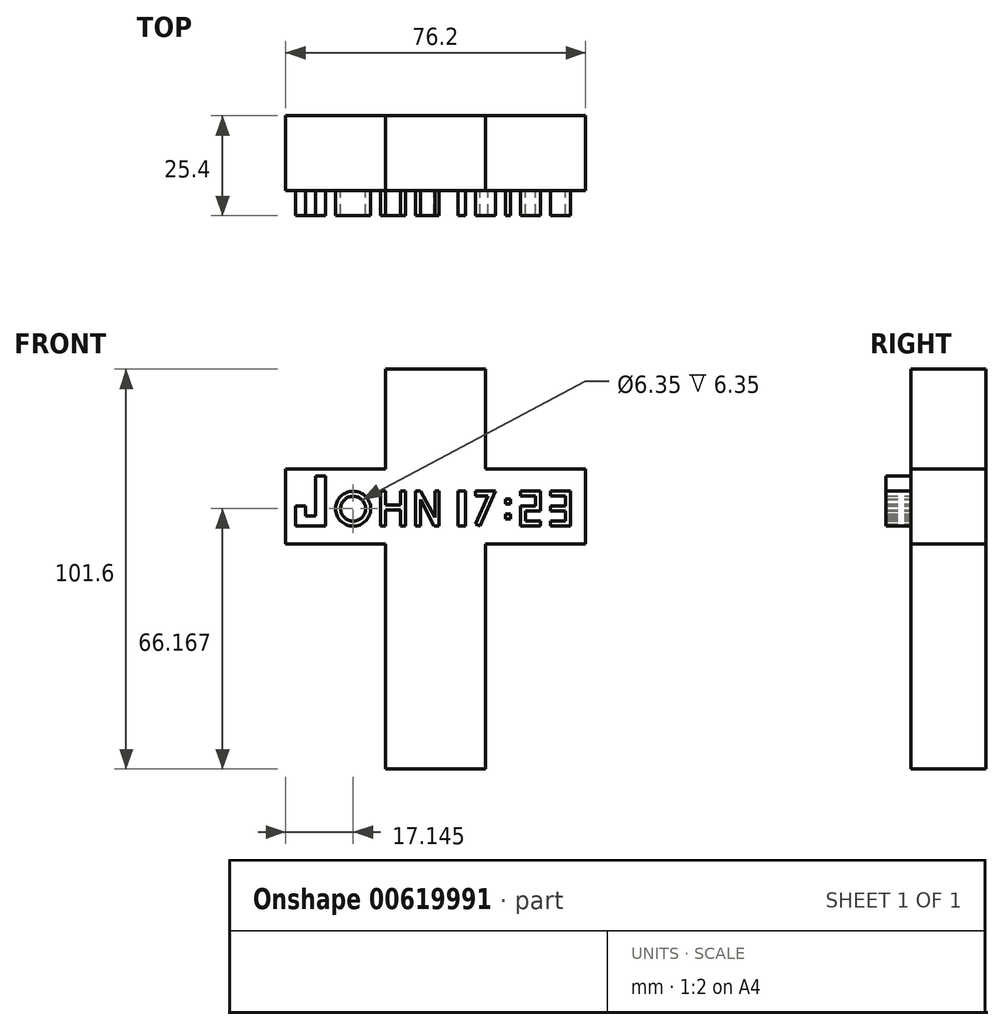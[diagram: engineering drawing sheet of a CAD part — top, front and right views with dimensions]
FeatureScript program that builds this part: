
annotation { "Feature Type Name" : "Feature", "Feature Type Description" : "" }
export const myFeature = defineFeature(function(context is Context, id is Id, definition is map)
    precondition{}
    {
        {
            var Q0;
            Q0=qCreatedBy(makeId("Front.planeOp"),FACE);
            var sketch = newSketch(context, id + "F0", { "sketchPlane" : qUnion([Q0])});
            skLineSegment(sketch, "E0", {"start": v(0, 0) * mm, "end": v(-25.4, 0) * mm});
            skLineSegment(sketch, "E1", {"start": v(-25.4, 0) * mm, "end": v(-25.4, 101.6) * mm});
            skLineSegment(sketch, "E2", {"start": v(-25.4, 101.6) * mm, "end": v(0, 101.6) * mm});
            skLineSegment(sketch, "E3", {"start": v(0, 101.6) * mm, "end": v(0, 0) * mm});
            skLineSegment(sketch, "E4", {"start": v(-25.4, 76.2) * mm, "end": v(-50.8, 76.2) * mm});
            skLineSegment(sketch, "E5", {"start": v(-50.8, 76.2) * mm, "end": v(-50.8, 57.15) * mm});
            skLineSegment(sketch, "E6", {"start": v(-50.8, 57.15) * mm, "end": v(-25.4, 57.15) * mm});
            skLineSegment(sketch, "E7", {"start": v(0, 76.2) * mm, "end": v(25.4, 76.2) * mm});
            skLineSegment(sketch, "E8", {"start": v(25.4, 76.2) * mm, "end": v(25.4, 57.15) * mm});
            skLineSegment(sketch, "E9", {"start": v(25.4, 57.15) * mm, "end": v(0, 57.15) * mm});
            skSolve(sketch);
        }
        {
            var Q0;
            Q0 = qSketchRegion(id + "F0", true);
            extrude(context, id + "F1", {"entities" : qUnion([Q0]), "depth" : 19.05 * mm, "offsetDistance" : 25.4 * mm});
        }
        {
            var Q0;
            Q0=qCreatedBy(makeId("Front.planeOp"),FACE);
            cPlane(context, id + "F2", {"entities" : qUnion([Q0]), "cplaneType" : CPlaneType.OFFSET, "offset" : 19.05 * mm, "width" : 152.4 * mm, "height" : 152.4 * mm});
        }
        {
            var Q0;
            Q0=qCreatedBy(id+"F2.planeOp",FACE);
            var sketch = newSketch(context, id + "F3", { "sketchPlane" : qUnion([Q0])});
            skLineSegment(sketch, "E10", {"start": v(-48.26, 66.8) * mm, "end": v(-45.72, 66.8) * mm});
            skLineSegment(sketch, "E11", {"start": v(-43.18, 74.42) * mm, "end": v(-40.64, 74.42) * mm});
            skLineSegment(sketch, "E12", {"start": v(-43.18, 74.42) * mm, "end": v(-43.18, 64.26) * mm});
            skLineSegment(sketch, "E13", {"start": v(-45.72, 66.8) * mm, "end": v(-45.72, 64.26) * mm});
            skLineSegment(sketch, "E14", {"start": v(-45.72, 64.26) * mm, "end": v(-43.18, 64.26) * mm});
            skLineSegment(sketch, "E15", {"start": v(-48.26, 66.8) * mm, "end": v(-48.26, 61.72) * mm});
            skLineSegment(sketch, "E16", {"start": v(-48.26, 61.72) * mm, "end": v(-40.64, 61.72) * mm});
            skLineSegment(sketch, "E17", {"start": v(-40.64, 74.42) * mm, "end": v(-40.64, 61.72) * mm});
            skSolve(sketch);
        }
        {
            var Q0;
            Q0=makeQuery(id+"F3.imprint","IMPRINT",FACE,{"disambiguationData":[TD([[makeQuery(id+"F3.imprint","IMPRINT",EDGE,{"derivedFrom":sQuery(id+"F3.wireOp",EDGE,"E10")}),-1.0]])]});
            extrude(context, id + "F4", {"entities" : qUnion([Q0]), "operationType" : NewBodyOperationType.ADD, "depth" : 6.35 * mm, "offsetDistance" : 25.4 * mm});
        }
        {
            var Q0;
            Q0=qCreatedBy(id+"F2.planeOp",FACE);
            var sketch = newSketch(context, id + "F5", { "sketchPlane" : qUnion([Q0])});
            skCircle(sketch, "E18", {"center": v(-33.66, 66.17) * mm, "radius": 4.45 * mm});
            skCircle(sketch, "E19", {"center": v(-33.66, 66.17) * mm, "radius": 3.17 * mm});
            skSolve(sketch);
        }
        {
            var Q0;
            Q0=makeQuery(id+"F5.imprint","IMPRINT",FACE,{"disambiguationData":[TD([[makeQuery(id+"F5.imprint","IMPRINT",EDGE,{"derivedFrom":sQuery(id+"F5.wireOp",EDGE,"E18")}),1.0]])]});
            extrude(context, id + "F6", {"entities" : qUnion([Q0]), "operationType" : NewBodyOperationType.ADD, "depth" : 6.35 * mm, "offsetDistance" : 25.4 * mm});
        }
        {
            var Q0;
            Q0=qCreatedBy(id+"F2.planeOp",FACE);
            var sketch = newSketch(context, id + "F7", { "sketchPlane" : qUnion([Q0])});
            skLineSegment(sketch, "E20", {"start": v(-26.67, 70.61) * mm, "end": v(-25.4, 70.61) * mm});
            skLineSegment(sketch, "E21", {"start": v(-25.4, 70.61) * mm, "end": v(-25.4, 61.72) * mm});
            skLineSegment(sketch, "E22", {"start": v(-25.4, 61.72) * mm, "end": v(-26.67, 61.72) * mm});
            skLineSegment(sketch, "E23", {"start": v(-26.67, 61.72) * mm, "end": v(-26.67, 70.61) * mm});
            skLineSegment(sketch, "E24", {"start": v(-25.4, 67.06) * mm, "end": v(-21.6, 67.06) * mm});
            skLineSegment(sketch, "E25", {"start": v(-21.6, 67.06) * mm, "end": v(-21.6, 65.79) * mm});
            skLineSegment(sketch, "E26", {"start": v(-21.6, 65.79) * mm, "end": v(-25.4, 65.79) * mm});
            skLineSegment(sketch, "E27", {"start": v(-21.6, 67.06) * mm, "end": v(-21.6, 70.61) * mm});
            skLineSegment(sketch, "E28", {"start": v(-21.6, 70.61) * mm, "end": v(-20.32, 70.61) * mm});
            skLineSegment(sketch, "E29", {"start": v(-20.32, 70.61) * mm, "end": v(-20.32, 61.72) * mm});
            skLineSegment(sketch, "E30", {"start": v(-20.32, 61.72) * mm, "end": v(-21.6, 61.72) * mm});
            skLineSegment(sketch, "E31", {"start": v(-21.6, 61.72) * mm, "end": v(-21.6, 65.79) * mm});
            skSolve(sketch);
        }
        {
            var Q0;
            Q0 = qSketchRegion(id + "F7", true);
            extrude(context, id + "F8", {"entities" : qUnion([Q0]), "operationType" : NewBodyOperationType.ADD, "depth" : 6.35 * mm, "offsetDistance" : 25.4 * mm});
        }
        {
            var Q0;
            Q0=qCreatedBy(id+"F2.planeOp",FACE);
            var sketch = newSketch(context, id + "F9", { "sketchPlane" : qUnion([Q0])});
            skLineSegment(sketch, "E32", {"start": v(-17.78, 61.72) * mm, "end": v(-17.78, 70.61) * mm});
            skLineSegment(sketch, "E33", {"start": v(-17.78, 70.61) * mm, "end": v(-16.51, 70.61) * mm});
            skLineSegment(sketch, "E34", {"start": v(-16.51, 70.61) * mm, "end": v(-16.51, 61.72) * mm});
            skLineSegment(sketch, "E35", {"start": v(-16.51, 61.72) * mm, "end": v(-17.78, 61.72) * mm});
            skLineSegment(sketch, "E36", {"start": v(-11.78, 61.72) * mm, "end": v(-13.05, 61.72) * mm});
            skLineSegment(sketch, "E37", {"start": v(-13.05, 61.72) * mm, "end": v(-16.51, 68.51) * mm});
            skLineSegment(sketch, "E38", {"start": v(-11.78, 61.72) * mm, "end": v(-11.78, 70.61) * mm});
            skLineSegment(sketch, "E39", {"start": v(-11.78, 70.61) * mm, "end": v(-12.92, 70.61) * mm});
            skLineSegment(sketch, "E40", {"start": v(-12.92, 70.61) * mm, "end": v(-12.92, 61.72) * mm});
            skLineSegment(sketch, "E41", {"start": v(-16.51, 70.61) * mm, "end": v(-12.92, 63.9) * mm});
            skSolve(sketch);
        }
        {
            var Q0;
            Q0 = qSketchRegion(id + "F9", true);
            extrude(context, id + "F10", {"entities" : qUnion([Q0]), "operationType" : NewBodyOperationType.ADD, "depth" : 6.35 * mm, "offsetDistance" : 25.4 * mm});
        }
        {
            var Q0;
            Q0=qCreatedBy(id+"F2.planeOp",FACE);
            var sketch = newSketch(context, id + "F11", { "sketchPlane" : qUnion([Q0])});
            skLineSegment(sketch, "E42", {"start": v(-6.97, 70.61) * mm, "end": v(-5.06, 70.61) * mm});
            skLineSegment(sketch, "E43", {"start": v(-5.06, 70.61) * mm, "end": v(-5.06, 61.72) * mm});
            skLineSegment(sketch, "E44", {"start": v(-5.06, 61.72) * mm, "end": v(-6.97, 61.72) * mm});
            skLineSegment(sketch, "E45", {"start": v(-6.97, 61.72) * mm, "end": v(-6.97, 70.61) * mm});
            skSolve(sketch);
        }
        {
            var Q0;
            Q0 = qSketchRegion(id + "F11", true);
            extrude(context, id + "F12", {"entities" : qUnion([Q0]), "operationType" : NewBodyOperationType.ADD, "depth" : 6.35 * mm, "offsetDistance" : 25.4 * mm});
        }
        {
            var Q0;
            Q0=qCreatedBy(id+"F2.planeOp",FACE);
            var sketch = newSketch(context, id + "F13", { "sketchPlane" : qUnion([Q0])});
            skLineSegment(sketch, "E46", {"start": v(-2.52, 70.61) * mm, "end": v(2.56, 70.61) * mm});
            skLineSegment(sketch, "E47", {"start": v(2.56, 70.61) * mm, "end": v(-1.42, 61.72) * mm});
            skLineSegment(sketch, "E48", {"start": v(-2.52, 70.61) * mm, "end": v(-2.52, 69.34) * mm});
            skLineSegment(sketch, "E49", {"start": v(-2.52, 69.34) * mm, "end": v(0.65, 69.34) * mm});
            skLineSegment(sketch, "E50", {"start": v(0.65, 69.34) * mm, "end": v(-2.52, 62.34) * mm});
            skLineSegment(sketch, "E51", {"start": v(-2.52, 62.34) * mm, "end": v(-1.42, 61.72) * mm});
            skSolve(sketch);
        }
        {
            var Q0;
            Q0 = qSketchRegion(id + "F13", true);
            extrude(context, id + "F14", {"entities" : qUnion([Q0]), "operationType" : NewBodyOperationType.ADD, "depth" : 6.35 * mm, "offsetDistance" : 25.4 * mm});
        }
        {
            var Q0;
            Q0=qCreatedBy(id+"F2.planeOp",FACE);
            var sketch = newSketch(context, id + "F15", { "sketchPlane" : qUnion([Q0])});
            skLineSegment(sketch, "E52.bottom", {"start": v(5.1, 68.58) * mm, "end": v(6.37, 68.58) * mm});
            skLineSegment(sketch, "E52.top", {"start": v(5.1, 67.31) * mm, "end": v(6.37, 67.31) * mm});
            skLineSegment(sketch, "E52.left", {"start": v(5.1, 68.58) * mm, "end": v(5.1, 67.31) * mm});
            skLineSegment(sketch, "E52.right", {"start": v(6.37, 68.58) * mm, "end": v(6.37, 67.31) * mm});
            skLineSegment(sketch, "E53.bottom", {"start": v(5.1, 64.77) * mm, "end": v(6.37, 64.77) * mm});
            skLineSegment(sketch, "E53.top", {"start": v(5.1, 63.5) * mm, "end": v(6.37, 63.5) * mm});
            skLineSegment(sketch, "E53.left", {"start": v(5.1, 64.77) * mm, "end": v(5.1, 63.5) * mm});
            skLineSegment(sketch, "E53.right", {"start": v(6.37, 64.77) * mm, "end": v(6.37, 63.5) * mm});
            skSolve(sketch);
        }
        {
            var Q0;
            Q0 = qSketchRegion(id + "F15", true);
            extrude(context, id + "F16", {"entities" : qUnion([Q0]), "operationType" : NewBodyOperationType.ADD, "depth" : 6.35 * mm, "offsetDistance" : 25.4 * mm});
        }
        {
            var Q0;
            Q0=qCreatedBy(id+"F2.planeOp",FACE);
            var sketch = newSketch(context, id + "F17", { "sketchPlane" : qUnion([Q0])});
            skLineSegment(sketch, "E54", {"start": v(8.9, 70.61) * mm, "end": v(13.99, 70.61) * mm});
            skLineSegment(sketch, "E55", {"start": v(13.99, 70.61) * mm, "end": v(13.99, 66.8) * mm});
            skLineSegment(sketch, "E56", {"start": v(13.99, 66.8) * mm, "end": v(8.9, 66.8) * mm});
            skLineSegment(sketch, "E57", {"start": v(8.9, 66.8) * mm, "end": v(8.9, 61.72) * mm});
            skLineSegment(sketch, "E58", {"start": v(8.9, 61.72) * mm, "end": v(13.99, 61.72) * mm});
            skLineSegment(sketch, "E59", {"start": v(13.99, 61.72) * mm, "end": v(13.99, 63) * mm});
            skLineSegment(sketch, "E60", {"start": v(13.99, 63) * mm, "end": v(10.18, 63) * mm});
            skLineSegment(sketch, "E61", {"start": v(10.18, 63) * mm, "end": v(10.18, 65.53) * mm});
            skLineSegment(sketch, "E62", {"start": v(10.18, 65.53) * mm, "end": v(13.99, 65.53) * mm});
            skLineSegment(sketch, "E63", {"start": v(13.99, 65.53) * mm, "end": v(13.99, 66.8) * mm});
            skLineSegment(sketch, "E64", {"start": v(8.9, 70.61) * mm, "end": v(8.9, 69.34) * mm});
            skLineSegment(sketch, "E65", {"start": v(8.9, 69.34) * mm, "end": v(12.72, 69.34) * mm});
            skLineSegment(sketch, "E66", {"start": v(12.72, 69.34) * mm, "end": v(12.72, 66.8) * mm});
            skSolve(sketch);
        }
        {
            var Q0;
            Q0 = qSketchRegion(id + "F17", true);
            extrude(context, id + "F18", {"entities" : qUnion([Q0]), "operationType" : NewBodyOperationType.ADD, "depth" : 6.35 * mm, "offsetDistance" : 25.4 * mm});
        }
        {
            var Q0;
            Q0=qCreatedBy(id+"F2.planeOp",FACE);
            var sketch = newSketch(context, id + "F19", { "sketchPlane" : qUnion([Q0])});
            skLineSegment(sketch, "E67", {"start": v(16.5, 69.34) * mm, "end": v(20.32, 69.34) * mm});
            skLineSegment(sketch, "E68", {"start": v(20.32, 65.53) * mm, "end": v(16.5, 65.53) * mm});
            skLineSegment(sketch, "E69", {"start": v(16.5, 65.53) * mm, "end": v(20.32, 65.53) * mm});
            skLineSegment(sketch, "E70", {"start": v(20.32, 61.72) * mm, "end": v(16.5, 61.72) * mm});
            skLineSegment(sketch, "E71", {"start": v(16.5, 61.72) * mm, "end": v(16.5, 63) * mm});
            skLineSegment(sketch, "E72", {"start": v(16.5, 63) * mm, "end": v(20.32, 63) * mm});
            skLineSegment(sketch, "E73", {"start": v(16.5, 65.53) * mm, "end": v(16.5, 66.8) * mm});
            skLineSegment(sketch, "E74", {"start": v(16.5, 66.8) * mm, "end": v(20.32, 66.8) * mm});
            skLineSegment(sketch, "E75", {"start": v(16.5, 69.34) * mm, "end": v(16.5, 70.61) * mm});
            skLineSegment(sketch, "E76", {"start": v(16.5, 70.61) * mm, "end": v(20.32, 70.61) * mm});
            skLineSegment(sketch, "E77", {"start": v(20.32, 70.61) * mm, "end": v(20.32, 69.34) * mm});
            skLineSegment(sketch, "E78", {"start": v(20.32, 70.61) * mm, "end": v(21.59, 70.61) * mm});
            skLineSegment(sketch, "E79", {"start": v(21.59, 70.61) * mm, "end": v(21.59, 61.72) * mm});
            skLineSegment(sketch, "E80", {"start": v(21.59, 61.72) * mm, "end": v(20.32, 61.72) * mm});
            skLineSegment(sketch, "E81", {"start": v(20.32, 61.72) * mm, "end": v(20.32, 63) * mm});
            skLineSegment(sketch, "E82", {"start": v(20.32, 65.53) * mm, "end": v(20.32, 63) * mm});
            skLineSegment(sketch, "E83", {"start": v(20.32, 65.53) * mm, "end": v(20.32, 66.8) * mm});
            skLineSegment(sketch, "E84", {"start": v(20.32, 69.34) * mm, "end": v(20.32, 66.8) * mm});
            skSolve(sketch);
        }
        {
            var Q0;
            Q0 = qSketchRegion(id + "F19", true);
            extrude(context, id + "F20", {"entities" : qUnion([Q0]), "operationType" : NewBodyOperationType.ADD, "depth" : 6.35 * mm, "offsetDistance" : 25.4 * mm});
        }
    });
